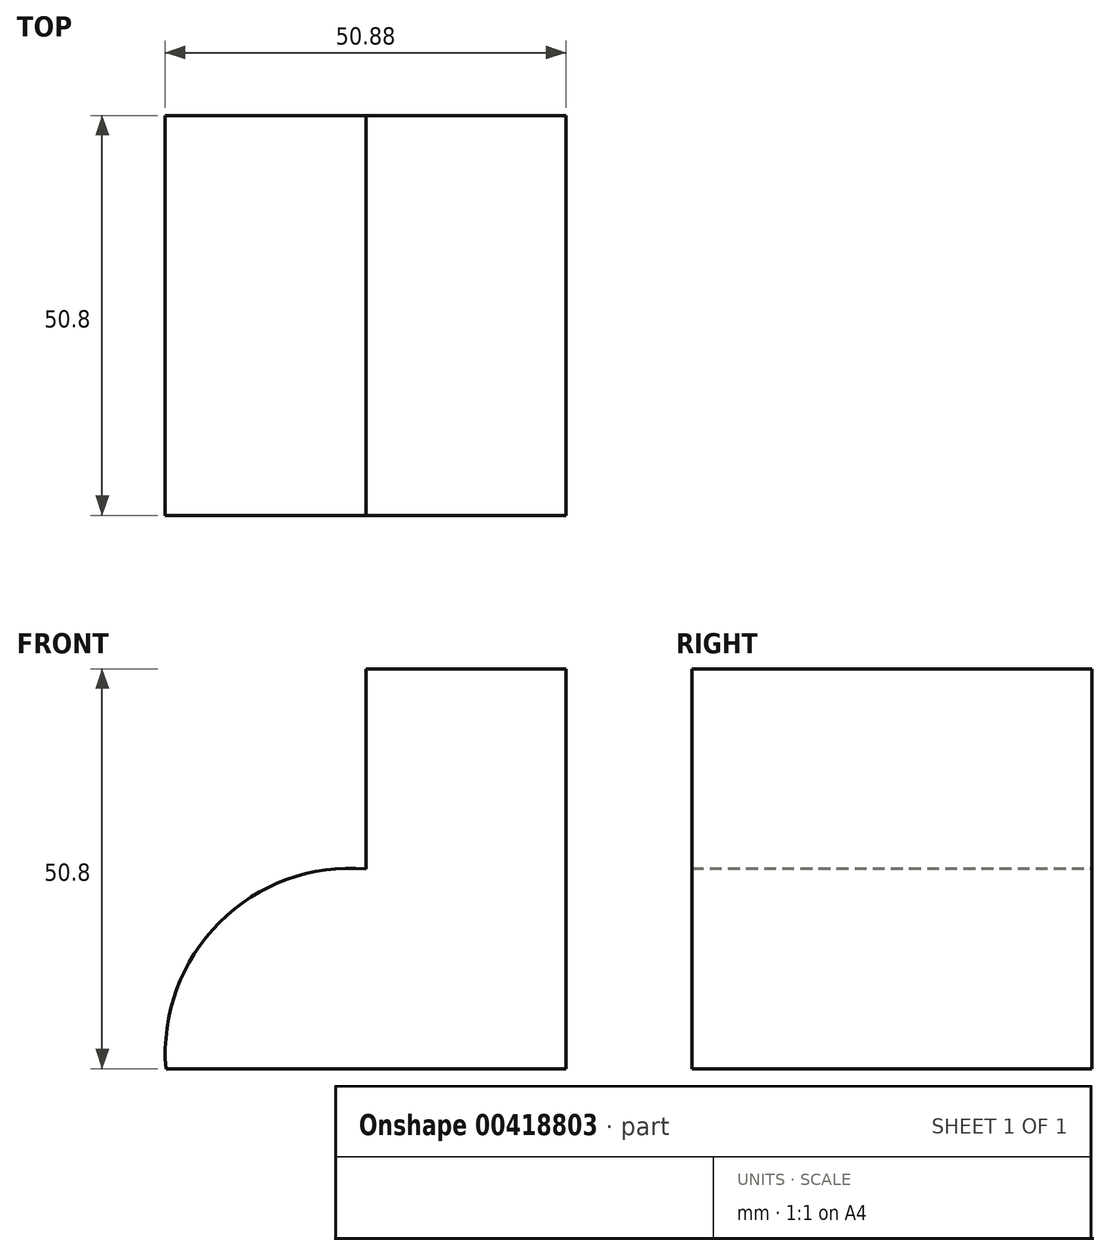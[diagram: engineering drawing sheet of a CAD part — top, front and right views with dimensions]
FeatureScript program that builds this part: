
annotation { "Feature Type Name" : "Feature", "Feature Type Description" : "" }
export const myFeature = defineFeature(function(context is Context, id is Id, definition is map)
    precondition{}
    {
        {
            var Q0;
            Q0=qCreatedBy(makeId("Front.planeOp"),FACE);
            var sketch = newSketch(context, id + "F0", { "sketchPlane" : qUnion([Q0])});
            skLineSegment(sketch, "E0", {"start": v(-55, 0) * mm, "end": v(-4.2, 0) * mm});
            skLineSegment(sketch, "E1", {"start": v(-4.2, 0) * mm, "end": v(-4.2, 50.8) * mm});
            skLineSegment(sketch, "E2", {"start": v(-4.2, 50.8) * mm, "end": v(-29.6, 50.8) * mm});
            skLineSegment(sketch, "E3", {"start": v(-29.6, 50.8) * mm, "end": v(-29.6, 25.4) * mm});
            skArc(sketch, "E4", {"start": v(-29.6, 25.4) * mm, "mid": v(-48.17, 18.58) * mm, "end": v(-55, 0) * mm});
            skSolve(sketch);
        }
        {
            var Q0;
            Q0=makeQuery(id+"F0.imprint","IMPRINT",FACE,{"disambiguationData":[TD([[makeQuery(id+"F0.imprint","IMPRINT",EDGE,{"derivedFrom":sQuery(id+"F0.wireOp",EDGE,"E0")}),1.0]])]});
            extrude(context, id + "F1", {"entities" : qUnion([Q0]), "depth" : 50.8 * mm});
        }
    });
